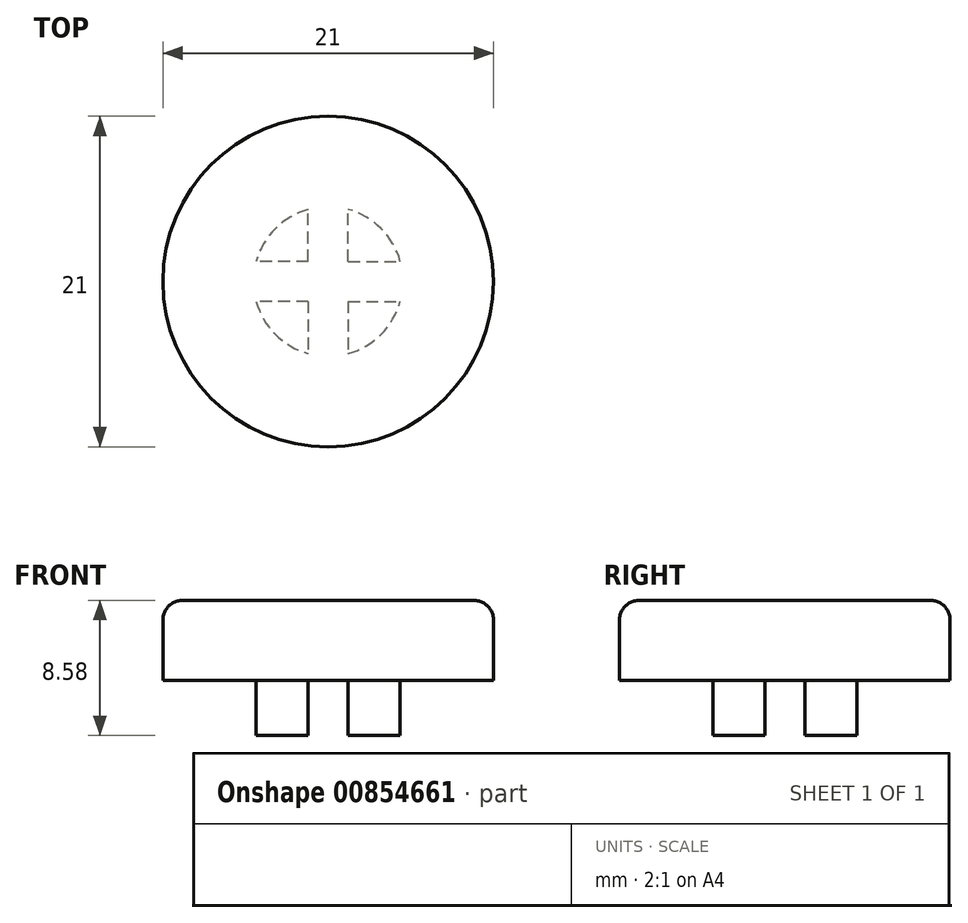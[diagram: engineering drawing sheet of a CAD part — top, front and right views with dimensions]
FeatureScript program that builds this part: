
annotation { "Feature Type Name" : "Feature", "Feature Type Description" : "" }
export const myFeature = defineFeature(function(context is Context, id is Id, definition is map)
    precondition{}
    {
        {
            var Q0;
            Q0=qCreatedBy(makeId("Top.planeOp"),FACE);
            var sketch = newSketch(context, id + "F0", { "sketchPlane" : qUnion([Q0])});
            skCircle(sketch, "E0", {"center": v(0, 0) * mm, "radius": 4.75 * mm});
            skSolve(sketch);
        }
        {
            var Q0;
            Q0=makeQuery(id+"F0.imprint","IMPRINT",FACE,{"disambiguationData":[TD([[makeQuery(id+"F0.imprint","IMPRINT",EDGE,{"derivedFrom":sQuery(id+"F0.wireOp",EDGE,"E0")}),1.0]])]});
            extrude(context, id + "F1", {"entities" : qUnion([Q0]), "depth" : 3.5 * mm, "offsetDistance" : 25.4 * mm});
        }
        {
            var Q0;
            Q0=makeQuery(id+"F1.opExtrude","CAP_FACE",FACE,{"disambiguationData":[OSD([sQuery(id+"F0.wireOp",EDGE,"E0")])],"isStart":false});
            var sketch = newSketch(context, id + "F2", { "sketchPlane" : qUnion([Q0])});
            skCircle(sketch, "E1", {"center": v(0, 0) * mm, "radius": 10.5 * mm});
            skSolve(sketch);
        }
        {
            var Q0;
            Q0=makeQuery(id+"F2.imprint","IMPRINT",FACE,{"disambiguationData":[TD([[makeQuery(id+"F2.imprint","IMPRINT",EDGE,{"derivedFrom":makeQuery(id+"F1.opExtrude","CAP_EDGE",EDGE,{"disambiguationData":[OSD([sQuery(id+"F0.wireOp",EDGE,"E0")])],"isStart":false})}),1.0]])]});
            var Q1;
            Q1=makeQuery(id+"F2.imprint","IMPRINT",FACE,{"disambiguationData":[TD([[makeQuery(id+"F2.imprint","IMPRINT",EDGE,{"derivedFrom":sQuery(id+"F2.wireOp",EDGE,"E1")}),1.0]])]});
            extrude(context, id + "F3", {"entities" : qUnion([Q0, Q1]), "operationType" : NewBodyOperationType.ADD, "depth" : 5.08 * mm, "offsetDistance" : 25.4 * mm});
        }
        {
            var Q0;
            Q0=makeQuery(id+"F3.opExtrude","CAP_EDGE",EDGE,{"disambiguationData":[OSD([sQuery(id+"F2.wireOp",EDGE,"E1")])],"isStart":false});
            fillet(context, id + "F4", {"entities" : qUnion([Q0]), "radius" : 1.27 * mm, "tangentPropagation" : true, "allowEdgeOverflow" : false});
        }
        {
            var Q0;
            Q0=makeQuery(id+"F3.opExtrude","CAP_FACE",FACE,{"disambiguationData":[OSD([sQuery(id+"F2.wireOp",EDGE,"E1")])],"isStart":true});
            var sketch = newSketch(context, id + "F5", { "sketchPlane" : qUnion([Q0])});
            skPoint(sketch, "E2.middle", {"position": v(0, 0) * mm});
            skLineSegment(sketch, "E3", {"start": v(0, 0) * mm, "end": v(1.27, 0) * mm, "construction": true});
            skLineSegment(sketch, "E4", {"start": v(0, 0) * mm, "end": v(-1.27, 0) * mm, "construction": true});
            skLineSegment(sketch, "E5", {"start": v(1.27, 0) * mm, "end": v(1.27, -10.42) * mm});
            skLineSegment(sketch, "E6", {"start": v(1.27, 0) * mm, "end": v(1.27, 10.42) * mm});
            skLineSegment(sketch, "E7", {"start": v(-1.27, 0) * mm, "end": v(-1.27, 10.42) * mm});
            skLineSegment(sketch, "E8", {"start": v(-1.27, 0) * mm, "end": v(-1.27, -10.42) * mm});
            skLineSegment(sketch, "E9", {"start": v(0, 0) * mm, "end": v(0, 1.27) * mm, "construction": true});
            skLineSegment(sketch, "E10", {"start": v(0, 0) * mm, "end": v(0, -1.27) * mm, "construction": true});
            skLineSegment(sketch, "E11", {"start": v(0, 1.27) * mm, "end": v(10.42, 1.27) * mm});
            skLineSegment(sketch, "E12", {"start": v(0, 1.27) * mm, "end": v(-10.42, 1.27) * mm});
            skLineSegment(sketch, "E13", {"start": v(0, -1.27) * mm, "end": v(-10.42, -1.27) * mm});
            skLineSegment(sketch, "E14", {"start": v(0, -1.27) * mm, "end": v(10.42, -1.27) * mm});
            skLineSegment(sketch, "E15", {"start": v(1.27, 10.42) * mm, "end": v(-1.27, 10.42) * mm});
            skLineSegment(sketch, "E16", {"start": v(-10.42, 1.27) * mm, "end": v(-10.42, -1.27) * mm});
            skLineSegment(sketch, "E17", {"start": v(1.27, -10.42) * mm, "end": v(-1.27, -10.42) * mm});
            skLineSegment(sketch, "E18", {"start": v(10.42, 1.27) * mm, "end": v(10.42, -1.27) * mm});
            skSolve(sketch);
        }
        {
            var Q0;
            Q0=qSketchRegion(id+"F5",true);
            extrude(context, id + "F6", {"entities" : qUnion([Q0]), "operationType" : NewBodyOperationType.REMOVE, "depth" : 25.4 * mm, "offsetDistance" : 25.4 * mm});
        }
    });
